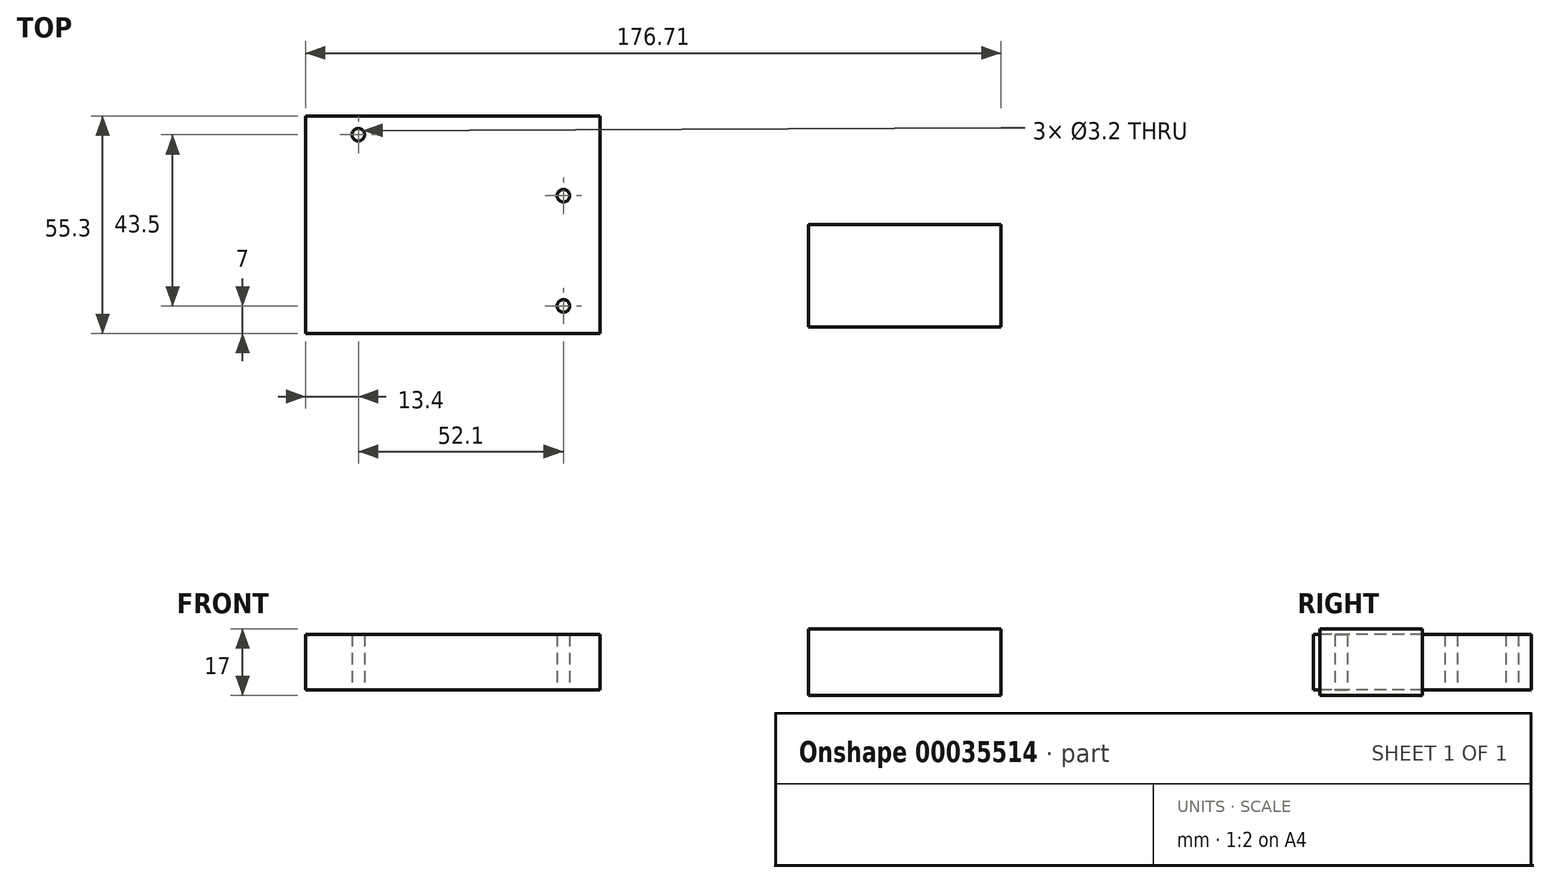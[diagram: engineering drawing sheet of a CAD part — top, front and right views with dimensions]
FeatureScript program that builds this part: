
annotation { "Feature Type Name" : "Feature", "Feature Type Description" : "" }
export const myFeature = defineFeature(function(context is Context, id is Id, definition is map)
    precondition{}
    {
        {
            var Q0;
            Q0=qCreatedBy(makeId("Top.planeOp"),FACE);
            var sketch = newSketch(context, id + "F0", { "sketchPlane" : qUnion([Q0])});
            skLineSegment(sketch, "E0.rect.bottom", {"start": v(37.4, 27.65) * mm, "end": v(-37.4, 27.65) * mm});
            skLineSegment(sketch, "E0.rect.top", {"start": v(37.4, -27.65) * mm, "end": v(-37.4, -27.65) * mm});
            skLineSegment(sketch, "E0.rect.left", {"start": v(37.4, 27.65) * mm, "end": v(37.4, -27.65) * mm});
            skLineSegment(sketch, "E0.rect.right", {"start": v(-37.4, 27.65) * mm, "end": v(-37.4, -27.65) * mm});
            skPoint(sketch, "E0.rect.middle", {"position": v(0, 0) * mm});
            skCircle(sketch, "E1", {"center": v(-24, 22.85) * mm, "radius": 1.6 * mm});
            skCircle(sketch, "E2", {"center": v(28.1, -20.65) * mm, "radius": 1.6 * mm});
            skCircle(sketch, "E3", {"center": v(28.1, 7.35) * mm, "radius": 1.6 * mm});
            skSolve(sketch);
        }
        {
            var Q0;
            Q0 = qSketchRegion(id + "F0", true);
            extrude(context, id + "F1", {"entities" : qUnion([Q0]), "endBound" : BoundingType.SYMMETRIC, "depth" : 14 * mm});
        }
        {
            var Q0;
            Q0=qCreatedBy(makeId("Top.planeOp"),FACE);
            var sketch = newSketch(context, id + "F2", { "sketchPlane" : qUnion([Q0])});
            skLineSegment(sketch, "E4.rect.bottom", {"start": v(139.31, 0) * mm, "end": v(90.31, 0) * mm});
            skLineSegment(sketch, "E4.rect.top", {"start": v(139.31, -26) * mm, "end": v(90.31, -26) * mm});
            skLineSegment(sketch, "E4.rect.left", {"start": v(139.31, 0) * mm, "end": v(139.31, -26) * mm});
            skLineSegment(sketch, "E4.rect.right", {"start": v(90.31, 0) * mm, "end": v(90.31, -26) * mm});
            skPoint(sketch, "E4.rect.middle", {"position": v(114.81, -13) * mm});
            skSolve(sketch);
        }
        {
            var Q0;
            Q0 = qSketchRegion(id + "F2", true);
            extrude(context, id + "F3", {"entities" : qUnion([Q0]), "endBound" : BoundingType.SYMMETRIC, "depth" : 17 * mm});
        }
    });
